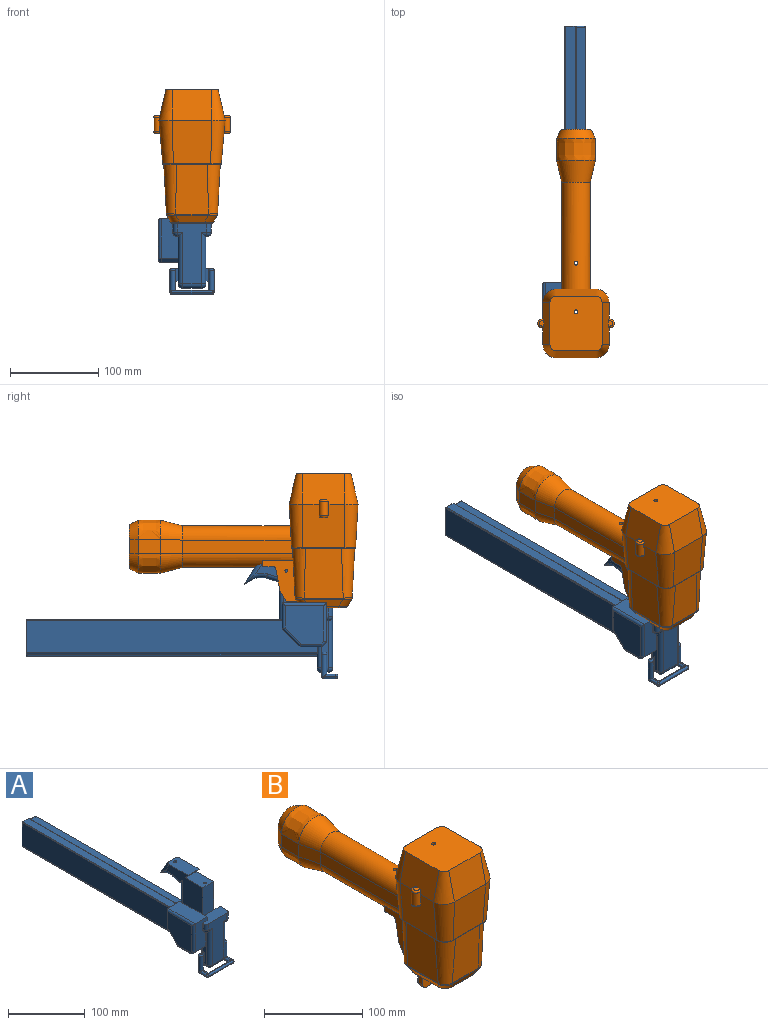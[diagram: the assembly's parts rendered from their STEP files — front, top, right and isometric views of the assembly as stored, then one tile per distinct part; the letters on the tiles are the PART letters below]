
ASSEMBLY  parts=2 mates=1
PART A: 171 faces, bbox 63.8x354.3x135.7 mm
  f0: plane 13.93x1.69mm, normal (0,1,0), area 2.9mm2, adj f37,f38,f52,f58,f169
  f1: plane 13.93x1.69mm, normal (0,1,0), area 2.9mm2, adj f3,f33,f52,f65,f168
  f2: plane 21.38x7.5mm, normal (0,0,-1), area 107.8mm2, adj f3,f8,f9,f38,f39,f43,f44,f158
  f3: cylinder r=5mm len=5mm, axis (-1,0,0), area 1.5mm2, adj f1,f2,f35,f168
  f4: plane 45.4x14.2mm, normal (0,0,-1), area 154.7mm2, adj f117,f130,f136,f137,f141,f142,f146,f147
  f5: plane 3x2.34mm, normal (0,0,1), area 0.2mm2, adj f115,f124,f125,f162
  f6: plane 45.4x10.28mm, normal (0,0,1), area 45.7mm2, adj f121,f124,f129,f134,f135,f143,f144,f145
  f7: plane 3x2.34mm, normal (0,0,1), area 0.2mm2, adj f111,f121,f126,f155
  f8: cylinder r=5mm len=5mm, axis (0,1,0), area 32.7mm2, adj f2,f29,f42,f163
  f9: cylinder r=5mm len=5mm, axis (0,-1,0), area 32.7mm2, adj f2,f31,f45,f157
  f10: cylinder r=1mm len=16.15mm, axis (0,1,0), area 25.2mm2, adj f13,f69,f72,f106
  f11: cylinder r=1mm len=267.15mm, axis (0,1,0), area 419.4mm2, adj f69,f71,f72,f106
  f12: cylinder r=20mm len=14.97mm, axis (1,0,0), area 140.3mm2, adj f93,f94,f99,f104,f105
  f13: plane 47.55x10mm, normal (0,1,0), area 470.7mm2, adj f10,f14,f15,f26,f54,f69,f72,f91
  f14: cylinder r=5mm len=51.66mm, axis (0,0,1), area 375.2mm2, adj f13,f25,f72,f91
  f15: cylinder r=5mm len=53.66mm, axis (0,0,-1), area 390.9mm2, adj f13,f54,f66,f91
  f16: plane 31.9x20mm, normal (0,0,1), area 624.2mm2, adj f23,f25,f66,f92,f108
  f17: plane 34.69x15.5mm, normal (0,1,0), area 512.4mm2, adj f19,f21,f28,f30,f33,f37,f50,f54
  f18: plane 10x1.89mm, normal (-1,0,0), area 18.9mm2, adj f19,f22,f32,f76
  f19: plane 43.38x17.5mm, normal (0,0,1), area 656.2mm2, adj f17,f18,f27,f28,f32,f48,f76,f78
  f20: plane 1.89x1mm, normal (0,0,-1), area 1.9mm2, adj f22,f29,f36,f76
  f21: plane 2.31x0.57mm, normal (0,0,-1), area 0.4mm2, adj f17,f33,f67,f77
  f22: cylinder r=5mm len=5mm, axis (0,-1,0), area 14.8mm2, adj f18,f20,f34,f76
  f23: plane 60.5x20mm, normal (0,-1,0), area 1200mm2, adj f16,f24,f25,f54,f66,f68,f69,f72
  f24: plane 37.5x1mm, normal (-1,0,0), area 37.5mm2, adj f23,f26,f54,f69
  f25: plane 68.89x65mm, normal (-1,0,0), area 2646.7mm2, adj f14,f16,f23,f72,f91,f92,f96,f97
  f26: cylinder r=5mm len=5mm, axis (0,0,1), area 7.9mm2, adj f13,f24,f54,f69
  f27: plane 68.5x33.38mm, normal (0,-1,0), area 1584.5mm2, adj f19,f32,f36,f40,f44,f46,f47,f48
  f28: plane 12.5x10mm, normal (1,0,0), area 125mm2, adj f17,f19,f48,f50
  f29: plane 53.5x7.5mm, normal (-1,0,0), area 230.2mm2, adj f8,f20,f33,f39,f40,f76,f80,f84
  f30: plane 12.5x6mm, normal (0,0,-1), area 17.9mm2, adj f17,f31,f37,f47,f50
  f31: plane 53.5x7.5mm, normal (1,0,0), area 383.2mm2, adj f9,f30,f37,f43,f46,f116,f119,f122
  f32: cylinder r=5mm len=10mm, axis (0,0,1), area 78.5mm2, adj f18,f19,f27,f34
  f33: cylinder r=5mm len=53.5mm, axis (0,0,1), area 259.3mm2, adj f1,f17,f21,f29,f35,f57,f77,f80
  f34: sphere r=5mm, area 39.3mm2, adj f22,f32,f36
  f35: sphere r=5mm, area 39.3mm2, adj f3,f33,f39
  f36: cylinder r=5mm len=6mm, axis (-1,0,0), area 22.1mm2, adj f20,f27,f34,f40
  f37: cylinder r=5mm len=53.5mm, axis (0,0,1), area 420.2mm2, adj f0,f17,f30,f31,f41,f51
  f38: cylinder r=5mm len=5mm, axis (-1,0,0), area 1.5mm2, adj f0,f2,f41,f169
  f39: cylinder r=5mm len=5mm, axis (0,1,0), area 18.4mm2, adj f2,f29,f35,f165
  f40: cylinder r=5mm len=58.5mm, axis (0,0,-1), area 434.5mm2, adj f27,f29,f36,f42
  f41: sphere r=5mm, area 39.3mm2, adj f37,f38,f43
  f42: sphere r=5mm, area 39.3mm2, adj f8,f40,f44
  f43: cylinder r=5mm len=5mm, axis (0,-1,0), area 18.4mm2, adj f2,f31,f41,f159
  f44: cylinder r=5mm len=21.38mm, axis (1,0,0), area 167.9mm2, adj f2,f27,f42,f45
  f45: sphere r=5mm, area 39.3mm2, adj f9,f44,f46
  f46: cylinder r=5mm len=58.5mm, axis (0,0,-1), area 434.5mm2, adj f27,f31,f45,f47
  f47: cylinder r=5mm len=6mm, axis (1,0,0), area 22.1mm2, adj f27,f30,f46,f49
  f48: cylinder r=5mm len=10mm, axis (0,0,1), area 78.5mm2, adj f19,f27,f28,f49
  f49: sphere r=5mm, area 39.3mm2, adj f47,f48,f50
  f50: cylinder r=5mm len=12.5mm, axis (0,1,0), area 98.2mm2, adj f17,f28,f30,f49
  f51: plane 39.07x0.31mm, normal (0,-1,0), area 12mm2, adj f37,f54,f55,f58
  f52: plane 335.5x21mm, normal (0,0,-1), area 6033.8mm2, adj f0,f1,f58,f62,f65,f107,f108,f168
  f53: plane 328x38mm, normal (-1,0,0), area 12464mm2, adj f54,f57,f63,f65
  f54: plane 328x22mm, normal (0,0,1), area 6362.9mm2, adj f13,f15,f17,f23,f24,f26,f51,f53
  f55: plane 328x38mm, normal (1,0,0), area 12464mm2, adj f51,f54,f58,f59
  f56: plane 36x18mm, normal (0,1,0), area 648mm2, adj f59,f61,f62,f63
  f57: plane 39.07x0.31mm, normal (0,-1,0), area 12mm2, adj f33,f53,f54,f65
  f58: cylinder r=2mm len=328mm, axis (0,-1,0), area 1030.4mm2, adj f0,f51,f52,f55,f60
  f59: cylinder r=2mm len=38mm, axis (0,0,1), area 116.2mm2, adj f55,f56,f60,f61
  f60: sphere r=2mm, area 6.3mm2, adj f58,f59,f62
  f61: cylinder r=2mm len=22mm, axis (-1,0,0), area 62.8mm2, adj f54,f56,f59,f63
  f62: cylinder r=2mm len=18mm, axis (1,0,0), area 56.5mm2, adj f52,f56,f60,f64
  f63: cylinder r=2mm len=38mm, axis (0,0,-1), area 116.2mm2, adj f53,f56,f61,f64
  f64: sphere r=2mm, area 6.3mm2, adj f62,f63,f65
  f65: cylinder r=2mm len=328mm, axis (0,1,0), area 1030.4mm2, adj f1,f52,f53,f57,f64
  f66: plane 68.89x67mm, normal (1,0,0), area 2721.7mm2, adj f15,f16,f23,f54,f91,f92,f96,f101
  f67: plane 37.5x1mm, normal (0,-1,0), area 37.3mm2, adj f21,f70,f73,f75,f77
  f68: plane 1x0.5mm, normal (1,0,0), area 0.5mm2, adj f17,f23,f69,f72
  f69: plane 330x12mm, normal (0,0,-1), area 3533.4mm2, adj f10,f11,f13,f17,f23,f24,f26,f68
  f70: plane 330x38mm, normal (1,0,0), area 12540mm2, adj f17,f67,f69,f71,f75
  f71: plane 39x13mm, normal (0,1,0), area 50.4mm2, adj f11,f69,f70,f72,f73,f74,f75
  f72: plane 330x12mm, normal (0,0,1), area 3250.5mm2, adj f10,f11,f13,f14,f17,f23,f25,f68
  f73: plane 330x37mm, normal (-1,0,0), area 11228.4mm2, adj f67,f71,f74,f75,f79,f80,f83
  f74: cylinder r=1mm len=330mm, axis (0,1,0), area 518.4mm2, adj f17,f71,f72,f73,f78
  f75: cylinder r=1mm len=330mm, axis (0,1,0), area 518.4mm2, adj f67,f70,f71,f73
  f76: plane 45x22mm, normal (0,-1,0), area 799.1mm2, adj f18,f19,f20,f22,f29,f78,f81,f84
  f77: plane 29.5x0.57mm, normal (1,0,0), area 16.7mm2, adj f21,f33,f67,f80
  f78: plane 50x20mm, normal (1,0,0), area 846.1mm2, adj f17,f19,f74,f76,f79,f81
  f79: plane 30x22mm, normal (0,1,0), area 660mm2, adj f73,f78,f81,f83,f85
  f80: plane 25x22mm, normal (0,0,-1), area 539.8mm2, adj f29,f33,f73,f77,f83,f84,f88
  f81: plane 50x22mm, normal (0,0,1), area 1100mm2, adj f76,f78,f79,f87
  f82: plane 44x44mm, normal (-1,0,0), area 1764.3mm2, adj f85,f86,f87,f88,f89,f90
  f83: plane 22x20mm, normal (0,0.71,-0.71), area 622.3mm2, adj f73,f79,f80,f86
  f84: plane 19.31x5mm, normal (0,-0.71,-0.71), area 136.5mm2, adj f29,f76,f80,f90
  f85: cylinder r=3mm len=30mm, axis (0,0,1), area 133.3mm2, adj f79,f82,f86,f87
  f86: cylinder r=3mm len=22.12mm, axis (0,0.71,0.71), area 127.4mm2, adj f82,f83,f85,f88
  f87: cylinder r=3mm len=50mm, axis (0,-1,0), area 225.3mm2, adj f81,f82,f85,f89
  f88: cylinder r=3mm len=25mm, axis (0,1,0), area 112mm2, adj f80,f82,f86,f90
  f89: cylinder r=3mm len=45mm, axis (0,0,-1), area 204mm2, adj f76,f82,f87,f90
  f90: cylinder r=3mm len=7.12mm, axis (0,-0.71,0.71), area 27.5mm2, adj f82,f84,f88,f89
  f91: plane 20x8.66mm, normal (0,-0.77,-0.63), area 71.1mm2, adj f13,f14,f15,f25,f66,f93,f97,f101
  f92: plane 20x6.5mm, normal (0,-0.77,-0.63), area 168mm2, adj f16,f25,f66,f96
  f93: plane 12.73x10mm, normal (0,0.28,-0.96), area 132.6mm2, adj f12,f91,f97,f101
  f94: plane 10x9.82mm, normal (0,-0.47,-0.88), area 111.2mm2, adj f12,f95,f100,f103
  f95: plane 25x15.52mm, normal (0,0.85,0.53), area 294.3mm2, adj f94,f96,f98,f102
  f96: plane 40x20mm, normal (0,0,1), area 773.5mm2, adj f25,f66,f92,f95,f98,f102,f105
  f97: cylinder r=5mm len=16.17mm, axis (0,-0.96,-0.28), area 110.2mm2, adj f25,f91,f93,f99
  f98: cylinder r=5mm len=30.28mm, axis (0,0.53,-0.85), area 188.6mm2, adj f25,f95,f96,f99,f100
  f99: torus R=25mm, axis (-1,0,0), area 126mm2, adj f12,f25,f97,f98,f100
  f100: cylinder r=5mm len=11.23mm, axis (0,0.88,-0.47), area 42mm2, adj f94,f98,f99
  f101: cylinder r=5mm len=16.17mm, axis (0,0.96,0.28), area 110.2mm2, adj f66,f91,f93,f104
  f102: cylinder r=5mm len=30.28mm, axis (0,-0.53,0.85), area 188.6mm2, adj f66,f95,f96,f103,f104
  f103: cylinder r=5mm len=11.23mm, axis (0,0.88,-0.47), area 42mm2, adj f94,f102,f104
  f104: torus R=25mm, axis (-1,0,0), area 126mm2, adj f12,f66,f101,f102,f103
  f105: cylinder r=2.1mm len=17.62mm, axis (0,0,-1), area 232.5mm2, adj f12,f96
  f106: cylinder r=2.1mm len=4.2mm, axis (0,0,-1), area 5.6mm2, adj f10,f11,f69,f72
  f107: cylinder r=2.1mm len=40mm, axis (0,0,-1), area 527.8mm2, adj f52,f54
  f108: cylinder r=2.1mm len=100.5mm, axis (0,0,-1), area 1326.1mm2, adj f16,f52
  f109: plane 15x6.07mm, normal (0,1,0), area 51.9mm2, adj f29,f123,f124,f127,f167
  f110: plane 15.76x6.46mm, normal (0,-1,0), area 51.1mm2, adj f29,f123,f124,f127,f167
  f111: plane 3x0.07mm, normal (0,1,0), area 0.2mm2, adj f7,f121,f126,f151
  f112: plane 13.2x0.4mm, normal (1,0,0), area 5.3mm2, adj f121,f135,f136,f140
  f113: plane 45.4x0.4mm, normal (0,-1,0), area 18.2mm2, adj f131,f134,f137,f140
  f114: plane 13.2x0.4mm, normal (-1,0,0), area 5.3mm2, adj f124,f129,f130,f131
  f115: plane 3x0.07mm, normal (0,1,0), area 0.2mm2, adj f5,f124,f125,f147
  f116: plane 15x6.07mm, normal (0,1,0), area 51.9mm2, adj f31,f121,f122,f128,f160
  f117: plane 42.6x2.7mm, normal (0,1,0), area 104.9mm2, adj f4,f118,f120,f141,f142,f144
  f118: plane 10.16x0.4mm, normal (-1,0,0), area 4.1mm2, adj f117,f141,f145,f154
  f119: plane 15.76x6.46mm, normal (0,-1,0), area 51.1mm2, adj f31,f121,f122,f128,f160
  f120: plane 10.16x0.4mm, normal (1,0,0), area 4.1mm2, adj f117,f142,f143,f161
  f121: cylinder r=3mm len=25.7mm, axis (0,0,-1), area 424.9mm2, adj f6,f7,f111,f112,f116,f119,f128,f135
  f122: plane 7.01x1.4mm, normal (0,0,1), area 7.2mm2, adj f31,f116,f119,f128
  f123: plane 7.01x1.4mm, normal (0,0,1), area 7.2mm2, adj f29,f109,f110,f127
  f124: cylinder r=3mm len=25.7mm, axis (0,0,-1), area 424.9mm2, adj f5,f6,f109,f110,f114,f115,f127,f129
  f125: cylinder r=3mm len=3mm, axis (0,0,-1), area 12.1mm2, adj f5,f115,f146,f162
  f126: cylinder r=3mm len=3mm, axis (0,0,-1), area 12.1mm2, adj f7,f111,f150,f155
  f127: torus R=0.7mm, axis (0,0,1), area 44.5mm2, adj f109,f110,f123,f124
  f128: torus R=0.7mm, axis (0,0,1), area 44.5mm2, adj f116,f119,f121,f122
  f129: cylinder r=2.3mm len=13.2mm, axis (0,-1,0), area 42.4mm2, adj f6,f114,f124,f132
  f130: cylinder r=2.3mm len=13.91mm, axis (0,1,0), area 49mm2, adj f4,f114,f133,f149
  f131: cylinder r=2.3mm len=2.3mm, axis (0,0,-1), area 1.4mm2, adj f113,f114,f132,f133
  f132: sphere r=2.3mm, area 8.3mm2, adj f129,f131,f134
  f133: sphere r=2.3mm, area 8.3mm2, adj f130,f131,f137
  f134: cylinder r=2.3mm len=45.4mm, axis (1,0,0), area 164mm2, adj f6,f113,f132,f138
  f135: cylinder r=2.3mm len=13.2mm, axis (0,1,0), area 42.4mm2, adj f6,f112,f121,f138
  f136: cylinder r=2.3mm len=13.91mm, axis (0,-1,0), area 49mm2, adj f4,f112,f139,f153
  f137: cylinder r=2.3mm len=45.4mm, axis (-1,0,0), area 164mm2, adj f4,f113,f133,f139
  f138: sphere r=2.3mm, area 8.3mm2, adj f134,f135,f140
  f139: sphere r=2.3mm, area 8.3mm2, adj f136,f137,f140
  f140: cylinder r=2.3mm len=2.3mm, axis (0,0,1), area 1.4mm2, adj f112,f113,f138,f139
  f141: cylinder r=2.3mm len=10.16mm, axis (0,1,0), area 36.7mm2, adj f4,f117,f118,f154
  f142: cylinder r=2.3mm len=10.16mm, axis (0,-1,0), area 36.7mm2, adj f4,f117,f120,f161
  f143: cylinder r=2.3mm len=12.46mm, axis (0,1,0), area 34.6mm2, adj f6,f120,f124,f144,f161
  f144: cylinder r=2.3mm len=42.6mm, axis (-1,0,0), area 143.3mm2, adj f6,f117,f143,f145
  f145: cylinder r=2.3mm len=12.46mm, axis (0,-1,0), area 34.6mm2, adj f6,f118,f121,f144,f154
  f146: torus R=1mm, axis (0,0,-1), area 9.1mm2, adj f4,f125,f147,f162
  f147: cylinder r=2mm len=2mm, axis (1,0,0), area 0.2mm2, adj f4,f115,f146,f148
  f148: torus R=1mm, axis (0,0,-1), area 5.5mm2, adj f4,f124,f147,f149
  f149: bspline ~2.88x2.62mm, area 4.3mm2, adj f124,f130,f148
  f150: torus R=1mm, axis (0,0,-1), area 9.1mm2, adj f4,f126,f151,f155
  f151: cylinder r=2mm len=2mm, axis (1,0,0), area 0.2mm2, adj f4,f111,f150,f152
  f152: torus R=1mm, axis (0,0,-1), area 5.5mm2, adj f4,f121,f151,f153
  f153: bspline ~2.88x2.62mm, area 4.3mm2, adj f121,f136,f152
  f154: plane 15x2.3mm, normal (0,1,0), area 33.1mm2, adj f118,f121,f141,f145,f156,f160
  f155: plane 15x2.17mm, normal (0,-1,0), area 31mm2, adj f7,f121,f126,f150,f156,f160
  f156: plane 15x1mm, normal (-0.99,-0.13,0), area 15.1mm2, adj f4,f154,f155,f160
  f157: plane 8x5mm, normal (0,1,0), area 34.6mm2, adj f9,f31,f158,f160
  f158: plane 8x1mm, normal (1,0,0), area 8mm2, adj f2,f157,f159,f160
  f159: plane 8x5mm, normal (0,-1,0), area 34.6mm2, adj f31,f43,f158,f160
  f160: plane 10.61x1mm, normal (0,0,-1), area 10.5mm2, adj f116,f119,f154,f155,f156,f157,f158,f159
  f161: plane 15x2.3mm, normal (0,1,0), area 33.1mm2, adj f120,f124,f142,f143,f164,f167
  f162: plane 15x2.17mm, normal (0,-1,0), area 31mm2, adj f5,f124,f125,f146,f164,f167
  f163: plane 8x5mm, normal (0,1,0), area 34.6mm2, adj f8,f29,f166,f167
  f164: plane 15x1mm, normal (0.99,-0.13,0), area 15.1mm2, adj f4,f161,f162,f167
  f165: plane 8x5mm, normal (0,-1,0), area 34.6mm2, adj f29,f39,f166,f167
  f166: plane 8x1mm, normal (-1,0,0), area 8mm2, adj f2,f163,f165,f167
  f167: plane 10.61x1mm, normal (0,0,-1), area 10.5mm2, adj f109,f110,f161,f162,f163,f164,f165,f166
  f168: plane 18x7.5mm, normal (1,0,0), area 129.6mm2, adj f1,f2,f3,f52,f170
  f169: plane 18x7.5mm, normal (-1,0,0), area 129.6mm2, adj f0,f2,f38,f52,f170
  f170: plane 21x18mm, normal (0,1,0), area 378mm2, adj f2,f52,f168,f169
PART B: 128 faces, bbox 89.6x260.8x168.8 mm
  f0: cylinder r=16mm len=125.49mm, axis (0,-1,0), area 5262.3mm2, adj f2,f3,f5,f6,f12,f13,f14,f87
  f1: cylinder r=16mm len=123.3mm, axis (0,-1,0), area 6183.7mm2, adj f56,f87,f88,f101,f117
  f2: plane 56.29x4.99mm, normal (0,1,-0.05), area 202.9mm2, adj f0,f7,f25,f46,f48,f87,f108
  f3: plane 56.29x4.99mm, normal (0,1,-0.05), area 202.9mm2, adj f0,f4,f7,f31,f50,f88,f107
  f4: cylinder r=3mm len=4.65mm, axis (-1,0,0), area 6.6mm2, adj f3,f18,f50,f107
  f5: plane 10.53x8.43mm, normal (0,0,-1), area 88.8mm2, adj f0,f12,f107,f109
  f6: plane 5.25x4.67mm, normal (0,1,0), area 10.4mm2, adj f0,f107,f109
  f7: plane 71.04x64.9mm, normal (0,0,-1), area 117.7mm2, adj f2,f3,f8,f15,f25,f26,f27,f28
  f8: cylinder r=1mm len=5.13mm, axis (1,0,0), area 7.8mm2, adj f7,f56,f65,f87
  f9: plane 28x12mm, normal (0,0,-1), area 336mm2, adj f10,f18,f107,f108
  f10: plane 28x12mm, normal (0,0.86,-0.5), area 389mm2, adj f9,f11,f107,f108
  f11: plane 28x25.58mm, normal (0,0.98,-0.19), area 729.9mm2, adj f10,f12,f107,f108
  f12: cylinder r=3mm len=28mm, axis (-1,0,0), area 93.7mm2, adj f0,f5,f11,f13,f107,f108
  f13: plane 10.53x8.43mm, normal (0,0,-1), area 88.8mm2, adj f0,f12,f108,f110
  f14: plane 5.25x4.67mm, normal (0,1,0), area 10.4mm2, adj f0,f108,f110
  f15: cylinder r=1mm len=5.13mm, axis (1,0,0), area 7.8mm2, adj f7,f56,f64,f88
  f16: plane 49.49x43.38mm, normal (0,0,-1), area 1910.6mm2, adj f32,f33,f34,f35,f36,f37,f38,f39
  f17: bspline ~48.72x27.58mm, area 157mm2, adj f18,f24,f38,f50,f52,f54
  f18: plane 37.31x7.88mm, normal (0,0.87,-0.5), area 206.6mm2, adj f4,f9,f17,f19,f36,f48,f107,f108
  f19: bspline ~55.21x48.72mm, area 157mm2, adj f18,f20,f34,f42,f44,f46
  f20: plane 43.8x7.85mm, normal (0.87,0,-0.48), area 352.4mm2, adj f19,f21,f32,f40
  f21: bspline ~55.21x48.72mm, area 157mm2, adj f20,f22,f33,f41,f43,f45
  f22: plane 37.31x7.88mm, normal (0,-0.87,-0.5), area 299.6mm2, adj f21,f23,f35,f47
  f23: bspline ~55.21x48.72mm, area 157.1mm2, adj f22,f24,f37,f49,f51,f53
  f24: plane 43.8x7.85mm, normal (-0.87,0,-0.48), area 352.4mm2, adj f17,f23,f39,f55
  f25: bspline ~58.23x57mm, area 1108.8mm2, adj f2,f7,f26,f44
  f26: plane 56.32x44.46mm, normal (1,0,-0.05), area 2394.3mm2, adj f7,f25,f27,f40,f41,f42
  f27: bspline ~58.23x57mm, area 1108.8mm2, adj f7,f26,f28,f43
  f28: plane 56.29x37.96mm, normal (0,-1,-0.05), area 2026.7mm2, adj f7,f27,f29,f45,f47,f49
  f29: bspline ~58.23x57mm, area 1108.8mm2, adj f7,f28,f30,f51
  f30: plane 56.31x44.45mm, normal (-1,0,-0.05), area 2394.3mm2, adj f7,f29,f31,f53,f54,f55
  f31: bspline ~58.23x57mm, area 1108.8mm2, adj f3,f7,f30,f52
  f32: cylinder r=3mm len=34.74mm, axis (0,1,0), area 111mm2, adj f16,f20,f33,f34,f80
  f33: bspline ~10.15x10.1mm, area 38.7mm2, adj f16,f21,f32,f35
  f34: bspline ~10.15x10.1mm, area 38.7mm2, adj f16,f19,f32,f36
  f35: cylinder r=3mm len=28.58mm, axis (1,0,0), area 89.8mm2, adj f16,f22,f33,f37
  f36: cylinder r=3mm len=28.58mm, axis (-1,0,0), area 89.8mm2, adj f16,f18,f34,f38
  f37: bspline ~10.15x10.1mm, area 38.7mm2, adj f16,f23,f35,f39
  f38: bspline ~10.15x10.1mm, area 38.7mm2, adj f16,f17,f36,f39
  f39: cylinder r=3mm len=34.74mm, axis (0,-1,0), area 111mm2, adj f16,f24,f37,f38,f72
  f40: cylinder r=3mm len=43.8mm, axis (0,1,0), area 59.6mm2, adj f20,f26,f41,f42
  f41: bspline ~1.37x0.76mm, area 0.5mm2, adj f21,f26,f40,f43
  f42: bspline ~1.37x0.76mm, area 0.5mm2, adj f19,f26,f40,f44
  f43: bspline ~10.22x10.13mm, area 27.1mm2, adj f21,f27,f41,f45
  f44: bspline ~10.2x10.16mm, area 27.1mm2, adj f19,f25,f42,f46
  f45: bspline ~1.46x1.18mm, area 0.5mm2, adj f21,f28,f43,f47
  f46: bspline ~1.46x1.18mm, area 0.5mm2, adj f2,f19,f44,f48
  f47: cylinder r=3mm len=37.31mm, axis (1,0,0), area 52.7mm2, adj f22,f28,f45,f49
  f48: cylinder r=3mm len=4.65mm, axis (-1,0,0), area 6.6mm2, adj f2,f18,f46,f108
  f49: bspline ~1.41x0.77mm, area 0.6mm2, adj f23,f28,f47,f51
  f50: bspline ~1.41x0.77mm, area 0.5mm2, adj f3,f4,f17,f52
  f51: bspline ~10.2x10.16mm, area 27.1mm2, adj f23,f29,f49,f53
  f52: bspline ~10.22x10.13mm, area 27.1mm2, adj f17,f31,f50,f54
  f53: bspline ~1.4x1.04mm, area 0.5mm2, adj f23,f30,f51,f55
  f54: bspline ~1.4x1.04mm, area 0.5mm2, adj f17,f30,f52,f55
  f55: cylinder r=3mm len=43.8mm, axis (0,-1,0), area 59.6mm2, adj f24,f30,f53,f54
  f56: plane 50.85x46.79mm, normal (0,1,-0.06), area 1466.5mm2, adj f1,f8,f15,f57,f63,f87,f88,f93
  f57: bspline ~60.94x50mm, area 1045.7mm2, adj f56,f58,f64,f94
  f58: plane 50.05x49.36mm, normal (-1,0,-0.09), area 2235.5mm2, adj f57,f59,f66,f95,f121,f122,f125
  f59: bspline ~60.94x50mm, area 1045.7mm2, adj f58,f60,f68,f96
  f60: plane 49.06x45mm, normal (0,-1,-0.06), area 2143.5mm2, adj f59,f61,f70,f97
  f61: bspline ~60.94x50mm, area 1045.7mm2, adj f60,f62,f69,f90
  f62: plane 50.05x49.36mm, normal (1,0,-0.09), area 2235.5mm2, adj f61,f63,f67,f91,f118,f119,f127
  f63: bspline ~49.09x16.37mm, area 1045.7mm2, adj f56,f62,f65,f92
  f64: bspline ~29.02x13.89mm, area 27.4mm2, adj f7,f15,f57,f66
  f65: bspline ~26.74x15.25mm, area 27.4mm2, adj f7,f8,f63,f67
  f66: cylinder r=1mm len=48.39mm, axis (0,1,0), area 71.8mm2, adj f7,f58,f64,f68
  f67: cylinder r=1mm len=48.39mm, axis (0,1,0), area 71.8mm2, adj f7,f62,f65,f69
  f68: bspline ~26.74x15.25mm, area 27.4mm2, adj f7,f59,f66,f70
  f69: bspline ~16.49x13.89mm, area 27.4mm2, adj f7,f61,f67,f70
  f70: cylinder r=1mm len=42.25mm, axis (1,0,0), area 64mm2, adj f7,f60,f68,f69
  f71: plane 6x3mm, normal (0,0,-1), area 18mm2, adj f74,f75,f81,f86
  f72: plane 10x6mm, normal (-1,0,0), area 60mm2, adj f39,f74,f84,f86
  f73: plane 10x9mm, normal (0,1,0), area 90mm2, adj f16,f75,f81,f84
  f74: plane 15x11mm, normal (0,-1,0), area 159.6mm2, adj f16,f71,f72,f75,f86
  f75: plane 15x8mm, normal (1,0,0), area 107.5mm2, adj f16,f71,f73,f74,f81
  f76: plane 6x3mm, normal (0,0,-1), area 18mm2, adj f77,f78,f82,f85
  f77: plane 15x11mm, normal (0,-1,0), area 159.6mm2, adj f16,f76,f78,f80,f85
  f78: plane 15x8mm, normal (-1,0,0), area 107.5mm2, adj f16,f76,f77,f79,f82
  f79: plane 10x9mm, normal (0,1,0), area 90mm2, adj f16,f78,f82,f83
  f80: plane 10x6mm, normal (1,0,0), area 60mm2, adj f32,f77,f83,f85
  f81: plane 11.41x5.56mm, normal (0,0.71,-0.71), area 69.1mm2, adj f71,f73,f75,f84,f86
  f82: plane 11.41x5.56mm, normal (0,0.71,-0.71), area 69.1mm2, adj f76,f78,f79,f83,f85
  f83: cylinder r=2mm len=11.23mm, axis (0,0,1), area 33.3mm2, adj f16,f79,f80,f82,f85
  f84: cylinder r=2mm len=11.23mm, axis (0,0,1), area 33.3mm2, adj f16,f72,f73,f81,f86
  f85: cylinder r=5mm len=6.77mm, axis (0,1,0), area 36.6mm2, adj f76,f77,f80,f82,f83
  f86: cylinder r=5mm len=6.77mm, axis (0,-1,0), area 36.6mm2, adj f71,f72,f74,f81,f84
  f87: plane 125.08x15mm, normal (1,0,0), area 1861.2mm2, adj f0,f1,f2,f7,f8,f56,f98
  f88: plane 125.08x15mm, normal (-1,0,0), area 1861.2mm2, adj f0,f1,f3,f7,f15,f56,f100
  f89: plane 62.49x59.49mm, normal (0,0,1), area 3602mm2, adj f90,f91,f92,f93,f94,f95,f96,f97
  f90: bspline ~63.41x35mm, area 620.3mm2, adj f61,f89,f91,f97
  f91: plane 48.76x35.76mm, normal (0.97,0,0.22), area 1676.8mm2, adj f62,f89,f90,f92,f118,f120,f126
  f92: bspline ~63.83x60.41mm, area 620.3mm2, adj f63,f89,f91,f93
  f93: plane 45x35mm, normal (0,0.97,0.22), area 1615.6mm2, adj f56,f89,f92,f94
  f94: bspline ~63.41x60.83mm, area 620.3mm2, adj f57,f89,f93,f95
  f95: plane 48.76x35.76mm, normal (-0.97,0,0.22), area 1676.8mm2, adj f58,f89,f94,f96,f121,f123,f124
  f96: bspline ~63.83x60.41mm, area 620.3mm2, adj f59,f89,f95,f97
  f97: plane 45x35mm, normal (0,-0.97,0.22), area 1615.6mm2, adj f60,f89,f90,f96
  f98: plane 25x16mm, normal (0.97,-0.23,0), area 398.5mm2, adj f87,f99,f101,f104
  f99: bspline ~44x27.7mm, area 1539.1mm2, adj f0,f98,f100,f105
  f100: plane 25x16mm, normal (-0.97,-0.23,0), area 398.5mm2, adj f88,f99,f101,f102
  f101: bspline ~44x27.7mm, area 1539.1mm2, adj f1,f98,f100,f103
  f102: plane 25x16mm, normal (-1,0,0), area 400mm2, adj f100,f103,f105,f113
  f103: extruded ~44x25mm, area 1728.1mm2, adj f101,f102,f104,f112
  f104: plane 25x16mm, normal (1,0,0), area 400mm2, adj f98,f103,f105,f115
  f105: extruded ~44x25mm, area 1728.1mm2, adj f99,f102,f104,f114
  f106: cylinder r=1.5mm len=28mm, axis (1,0,0), area 263.9mm2, adj f107,f108
  f107: plane 47.25x39.5mm, normal (-1,0,0), area 932.7mm2, adj f0,f3,f4,f5,f6,f9,f10,f11
  f108: plane 47.25x39.5mm, normal (1,0,0), area 932.7mm2, adj f0,f2,f9,f10,f11,f12,f13,f14
  f109: cylinder r=2mm len=8.43mm, axis (-1,0,0), area 20.6mm2, adj f0,f5,f6,f107
  f110: cylinder r=2mm len=8.43mm, axis (-1,0,0), area 20.6mm2, adj f0,f13,f14,f108
  f111: plane 50.66x34.66mm, normal (0,1,0), area 1451.9mm2, adj f112,f113,f114,f115
  f112: bspline ~44x21.99mm, area 684.9mm2, adj f103,f111,f113,f115
  f113: plane 16x10mm, normal (-0.89,0.45,0), area 178.9mm2, adj f102,f111,f112,f114
  f114: bspline ~44x38.67mm, area 684.9mm2, adj f105,f111,f113,f115
  f115: plane 16x10mm, normal (0.89,0.45,0), area 178.9mm2, adj f104,f111,f112,f114
  f116: cylinder r=2.1mm len=152mm, axis (0,0,-1), area 2005.6mm2, adj f16,f89
  f117: cylinder r=2.1mm len=46.72mm, axis (0,0,-1), area 616.5mm2, adj f0,f1
  f118: cylinder r=5mm len=16mm, axis (0,0,1), area 301.4mm2, adj f62,f91,f126,f127
  f119: plane 6x5.32mm, normal (0,0,-1), area 26.5mm2, adj f62,f127
  f120: plane 6x5.14mm, normal (0,0,1), area 25.8mm2, adj f91,f126
  f121: cylinder r=5mm len=16mm, axis (0,0,1), area 301.4mm2, adj f58,f95,f124,f125
  f122: plane 6x5.32mm, normal (0,0,-1), area 26.5mm2, adj f58,f125
  f123: plane 6x5.14mm, normal (0,0,1), area 25.8mm2, adj f95,f124
  f124: torus R=3mm, axis (0,0,1), area 57mm2, adj f95,f121,f123
  f125: torus R=3mm, axis (0,0,1), area 59.5mm2, adj f58,f121,f122
  f126: torus R=3mm, axis (0,0,1), area 57mm2, adj f91,f118,f120
  f127: torus R=3mm, axis (0,0,1), area 59.5mm2, adj f62,f118,f119
PLACE A at identity
PLACE B at identity fixed
MATE fastened A.f17 <-> B.f77  axis (0,1,0) through (21.69,7.34,-27.4)mm
